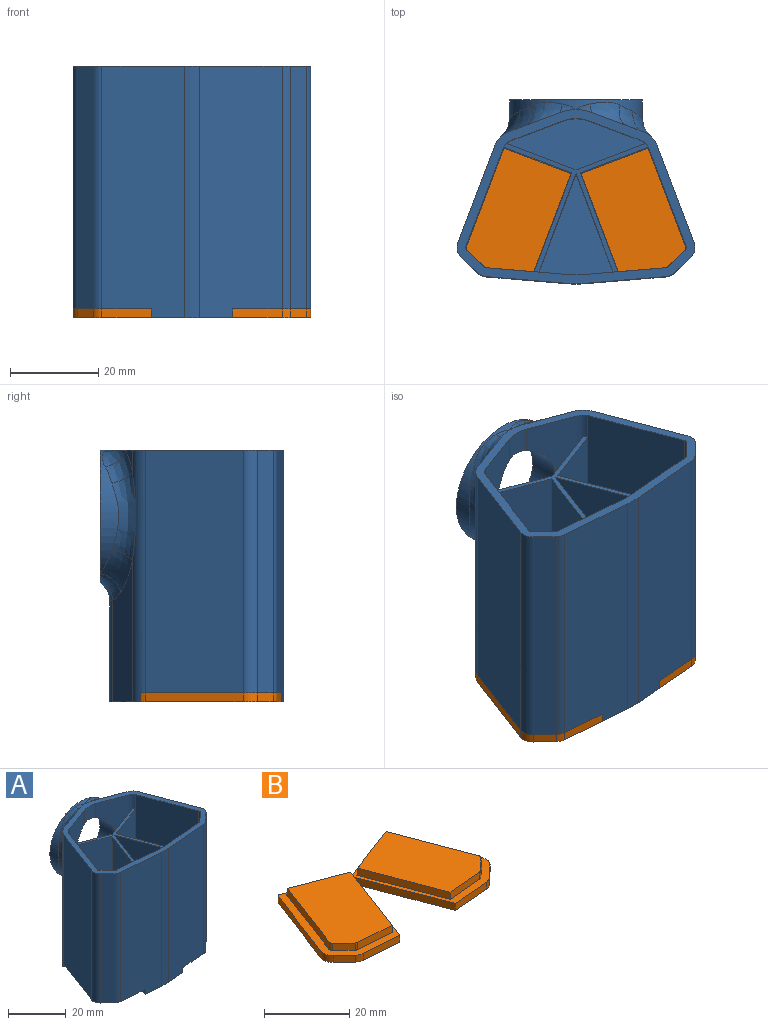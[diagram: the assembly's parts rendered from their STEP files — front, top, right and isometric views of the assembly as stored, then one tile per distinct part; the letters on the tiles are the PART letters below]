
ASSEMBLY  parts=2 mates=1
PART A: 70 faces, bbox 55x42.7x58 mm
  f0: plane 4.83x3.99mm, normal (-0.35,0.94,0), area 9.2mm2, adj f16,f45,f59
  f1: plane 31.83x11.97mm, normal (0.35,0.94,0), area 333.1mm2, adj f2,f44,f46,f64,f65
  f2: cylinder r=10mm len=23.06mm, axis (0,0,-1), area 165mm2, adj f1,f4,f46,f63
  f3: plane 4.83x3.99mm, normal (0.35,0.94,0), area 9.2mm2, adj f44,f45,f68
  f4: plane 31.83x11.97mm, normal (-0.35,0.94,0), area 333.1mm2, adj f2,f16,f46,f61,f62
  f5: cylinder r=8mm len=30.91mm, axis (0,0,-1), area 177mm2, adj f13,f14,f49,f54
  f6: cylinder r=8mm len=5.92mm, axis (0,0,-1), area 33.9mm2, adj f13,f14,f45,f54
  f7: cylinder r=18mm len=54.99mm, axis (0,0,-1), area 165.6mm2, adj f8,f9,f45,f53
  f8: plane 55x18.79mm, normal (0.08,1,0), area 986mm2, adj f7,f10,f15,f28,f38,f39,f45,f53
  f9: plane 55x18.79mm, normal (-0.08,1,0), area 986mm2, adj f7,f10,f15,f29,f34,f42,f45,f53
  f10: plane 54x31.91mm, normal (0,0,-1), area 264.3mm2, adj f8,f9,f16,f17,f18,f19,f20,f21
  f11: cylinder r=3mm len=54.99mm, axis (0,0,-1), area 74.8mm2, adj f14,f15,f30,f35,f45,f49
  f12: cylinder r=3mm len=54.99mm, axis (0,0,-1), area 74.8mm2, adj f13,f15,f36,f37,f45,f49
  f13: plane 54.99x11.97mm, normal (0.35,-0.94,0), area 607.3mm2, adj f5,f6,f12,f45,f49,f54
  f14: plane 54.99x11.97mm, normal (-0.35,-0.94,0), area 607.3mm2, adj f5,f6,f11,f45,f49,f54
  f15: plane 32.84x29.21mm, normal (0,0,1), area 82.2mm2, adj f8,f9,f11,f12,f28,f29,f30,f35
  f16: cylinder r=5mm len=57mm, axis (0,0,-1), area 218.3mm2, adj f0,f4,f10,f17,f45,f46,f48,f60
  f17: plane 55x22.2mm, normal (-0.94,0.35,0), area 1305.5mm2, adj f10,f16,f18,f45
  f18: cylinder r=3mm len=55mm, axis (0,0,-1), area 193.8mm2, adj f10,f17,f19,f45
  f19: plane 55x3.79mm, normal (-0.69,-0.73,0), area 286.8mm2, adj f10,f18,f20,f45
  f20: cylinder r=3mm len=55mm, axis (0,0,-1), area 111.3mm2, adj f10,f19,f21,f45
  f21: plane 57x18.79mm, normal (-0.08,-1,0), area 1052.2mm2, adj f10,f20,f22,f45,f50,f52
  f22: cylinder r=20mm len=57mm, axis (0,0,-1), area 190.7mm2, adj f21,f23,f45,f50
  f23: plane 57x18.79mm, normal (0.08,-1,0), area 1052.2mm2, adj f10,f22,f24,f45,f50,f51
  f24: cylinder r=3mm len=55mm, axis (0,0,-1), area 111.3mm2, adj f10,f23,f25,f45
  f25: plane 55x3.79mm, normal (0.69,-0.73,0), area 286.8mm2, adj f10,f24,f26,f45
  f26: cylinder r=3mm len=55mm, axis (0,0,-1), area 193.8mm2, adj f10,f25,f27,f45
  f27: plane 55x22.2mm, normal (0.94,0.35,0), area 1305.5mm2, adj f10,f26,f44,f45
  f28: plane 48.99x22.35mm, normal (0.94,-0.35,0), area 1170.7mm2, adj f8,f15,f29,f53
  f29: plane 48.99x22.35mm, normal (-0.94,-0.35,0), area 1170.7mm2, adj f9,f15,f28,f53
  f30: plane 55x15.43mm, normal (0.35,-0.94,0), area 808.6mm2, adj f10,f11,f15,f31,f42,f45
  f31: plane 55x22.45mm, normal (-0.94,-0.35,0), area 1320.2mm2, adj f10,f30,f32,f45
  f32: cylinder r=1mm len=55mm, axis (0,0,-1), area 64.6mm2, adj f10,f31,f33,f45
  f33: plane 55x3.79mm, normal (-0.69,0.73,0), area 286.8mm2, adj f10,f32,f34,f45
  f34: cylinder r=1mm len=55mm, axis (0,0,-1), area 37.1mm2, adj f9,f10,f33,f45
  f35: plane 48.99x15.81mm, normal (-0.35,0.94,0), area 828.4mm2, adj f11,f15,f36,f49
  f36: plane 48.99x15.81mm, normal (0.35,0.94,0), area 828.4mm2, adj f12,f15,f35,f49
  f37: plane 55x15.43mm, normal (-0.35,-0.94,0), area 808.6mm2, adj f10,f12,f15,f38,f43,f45
  f38: plane 49x22.44mm, normal (-0.94,0.35,0), area 1176mm2, adj f8,f10,f15,f37
  f39: cylinder r=1mm len=55mm, axis (0,0,-1), area 37.1mm2, adj f8,f10,f40,f45
  f40: plane 55x3.79mm, normal (0.69,0.73,0), area 286.8mm2, adj f10,f39,f41,f45
  f41: cylinder r=1mm len=55mm, axis (0,0,-1), area 64.6mm2, adj f10,f40,f43,f45
  f42: plane 49x22.44mm, normal (0.94,0.35,0), area 1176mm2, adj f9,f10,f15,f30
  f43: plane 55x22.45mm, normal (0.94,-0.35,0), area 1320.2mm2, adj f10,f37,f41,f45
  f44: cylinder r=5mm len=57mm, axis (0,0,-1), area 218.3mm2, adj f1,f3,f10,f27,f45,f46,f47,f66
  f45: plane 54.98x40.49mm, normal (0,0,1), area 290mm2, adj f0,f3,f6,f7,f8,f9,f11,f12
  f46: plane 35.59x13.63mm, normal (0,0,-1), area 268.1mm2, adj f1,f2,f4,f16,f44,f47,f48
  f47: plane 17.79x6.74mm, normal (0.35,-0.94,0), area 38.1mm2, adj f10,f44,f46,f48
  f48: plane 17.79x6.74mm, normal (-0.35,-0.94,0), area 38.1mm2, adj f10,f16,f46,f47
  f49: plane 31.63x11.63mm, normal (0,0,1), area 195.6mm2, adj f5,f11,f12,f13,f14,f35,f36
  f50: plane 25x18.4mm, normal (0,0,-1), area 230.5mm2, adj f21,f22,f23,f51,f52
  f51: plane 24.29x9.2mm, normal (0.94,0.35,0), area 52mm2, adj f10,f23,f50,f52
  f52: plane 24.29x9.2mm, normal (-0.94,0.35,0), area 52mm2, adj f10,f21,f50,f51
  f53: plane 23x16.93mm, normal (0,0,1), area 195.1mm2, adj f7,f8,f9,f28,f29
  f54: cylinder r=9.5mm len=19mm, axis (0,1,0), area 361.2mm2, adj f5,f6,f13,f14,f55
  f55: plane 30.11x30.11mm, normal (0,1,0), area 423.3mm2, adj f54,f56,f62,f63,f64
  f56: cylinder r=15mm len=30mm, axis (0,1,0), area 149.2mm2, adj f55,f57,f58,f59,f60,f61,f65,f66
  f57: bspline ~3.64x2.02mm, area 2.2mm2, adj f45,f56,f58
  f58: bspline ~9.98x5.59mm, area 30.9mm2, adj f45,f56,f57,f59
  f59: bspline ~7.37x6.18mm, area 36.2mm2, adj f0,f56,f58,f60
  f60: bspline ~22.1x5.77mm, area 92.5mm2, adj f16,f56,f59,f61
  f61: bspline ~9.63x8.2mm, area 59.9mm2, adj f4,f56,f60,f62
  f62: bspline ~7.27x6.41mm, area 28mm2, adj f4,f55,f61,f63
  f63: bspline ~8.02x4.71mm, area 37.3mm2, adj f2,f55,f62,f64
  f64: bspline ~7.27x6.41mm, area 28mm2, adj f1,f55,f63,f65
  f65: bspline ~9.63x8.2mm, area 59.9mm2, adj f1,f56,f64,f66
  f66: bspline ~22.1x5.77mm, area 92.5mm2, adj f44,f56,f65,f68
  f67: bspline ~3.66x2.03mm, area 2.2mm2, adj f45,f56,f69
  f68: bspline ~7.37x6.18mm, area 36.2mm2, adj f3,f56,f66,f69
  f69: bspline ~9.98x5.59mm, area 30.9mm2, adj f45,f56,f67,f68
PART B: 34 faces, bbox 54x31.9x4 mm
  f0: plane 53.99x31.91mm, normal (0,0,1), area 264.3mm2, adj f1,f2,f3,f4,f5,f6,f7,f8
  f1: cylinder r=5mm len=2mm, axis (0,0,1), area 2.6mm2, adj f0,f2,f16,f17
  f2: plane 17.79x6.74mm, normal (0.35,0.94,0), area 38.1mm2, adj f0,f1,f3,f17
  f3: plane 17.79x6.74mm, normal (-0.35,0.94,0), area 38.1mm2, adj f0,f2,f4,f17
  f4: cylinder r=5mm len=2mm, axis (0,0,1), area 2.6mm2, adj f0,f3,f5,f17
  f5: plane 22.2x8.41mm, normal (0.94,0.35,0), area 47.5mm2, adj f0,f4,f6,f17
  f6: cylinder r=3mm len=3.24mm, axis (0,0,1), area 7mm2, adj f0,f5,f7,f17
  f7: plane 3.79x3.59mm, normal (0.69,-0.73,0), area 10.4mm2, adj f0,f6,f8,f17
  f8: cylinder r=3mm len=2mm, axis (0,0,1), area 4mm2, adj f0,f7,f9,f17
  f9: plane 11.26x2mm, normal (0.08,-1,0), area 22.6mm2, adj f0,f8,f10,f17
  f10: plane 24.29x9.2mm, normal (-0.94,-0.35,0), area 52mm2, adj f0,f9,f11,f17
  f11: plane 24.29x9.2mm, normal (0.94,-0.35,0), area 52mm2, adj f0,f10,f12,f17
  f12: plane 11.26x2mm, normal (-0.08,-1,0), area 22.6mm2, adj f0,f11,f13,f17
  f13: cylinder r=3mm len=2mm, axis (0,0,1), area 4mm2, adj f0,f12,f14,f17
  f14: plane 3.79x3.59mm, normal (-0.69,-0.73,0), area 10.4mm2, adj f0,f13,f15,f17
  f15: cylinder r=3mm len=3.24mm, axis (0,0,1), area 7mm2, adj f0,f14,f16,f17
  f16: plane 22.2x8.41mm, normal (-0.94,0.35,0), area 47.5mm2, adj f0,f1,f15,f17
  f17: plane 53.99x31.91mm, normal (0,0,-1), area 1110.7mm2, adj f1,f2,f3,f4,f5,f6,f7,f8
  f18: cone r=1mm half-angle=3deg, axis (0,0,-1), area 1.3mm2, adj f0,f19,f24,f25
  f19: plane 10.79x2mm, normal (0.08,-1,0.05), area 21.6mm2, adj f0,f18,f20,f25
  f20: plane 22.44x8.57mm, normal (-0.93,-0.35,0.05), area 47.9mm2, adj f0,f19,f21,f25
  f21: plane 15.43x5.9mm, normal (-0.35,0.93,0.05), area 32.8mm2, adj f0,f20,f22,f25
  f22: plane 22.48x8.56mm, normal (0.93,0.35,0.05), area 48mm2, adj f0,f21,f23,f25
  f23: cone r=1mm half-angle=3deg, axis (0,0,-1), area 2.2mm2, adj f0,f22,f24,f25
  f24: plane 3.86x3.66mm, normal (0.69,-0.73,0.05), area 10.4mm2, adj f0,f18,f23,f25
  f25: plane 28.04x23.76mm, normal (0,0,1), area 414.6mm2, adj f18,f19,f20,f21,f22,f23,f24
  f26: cone r=1mm half-angle=3deg, axis (0,0,-1), area 2.2mm2, adj f0,f27,f32,f33
  f27: plane 22.48x8.56mm, normal (-0.93,0.35,0.05), area 48mm2, adj f0,f26,f28,f33
  f28: plane 15.43x5.9mm, normal (0.35,0.93,0.05), area 32.8mm2, adj f0,f27,f29,f33
  f29: plane 22.44x8.57mm, normal (0.93,-0.35,0.05), area 47.9mm2, adj f0,f28,f30,f33
  f30: plane 10.79x2mm, normal (-0.08,-1,0.05), area 21.6mm2, adj f0,f29,f31,f33
  f31: cone r=1mm half-angle=3deg, axis (0,0,-1), area 1.3mm2, adj f0,f30,f32,f33
  f32: plane 3.86x3.66mm, normal (-0.69,-0.73,0.05), area 10.4mm2, adj f0,f26,f31,f33
  f33: plane 28.04x23.76mm, normal (0,0,1), area 414.6mm2, adj f26,f27,f28,f29,f30,f31,f32
PLACE A t=(0,-6.81,2)mm
PLACE B t=(0,-6.81,44)mm
MATE slider B.f0 <-> A.f10  axis (0,0,1) through (0,17.32,2)mm
